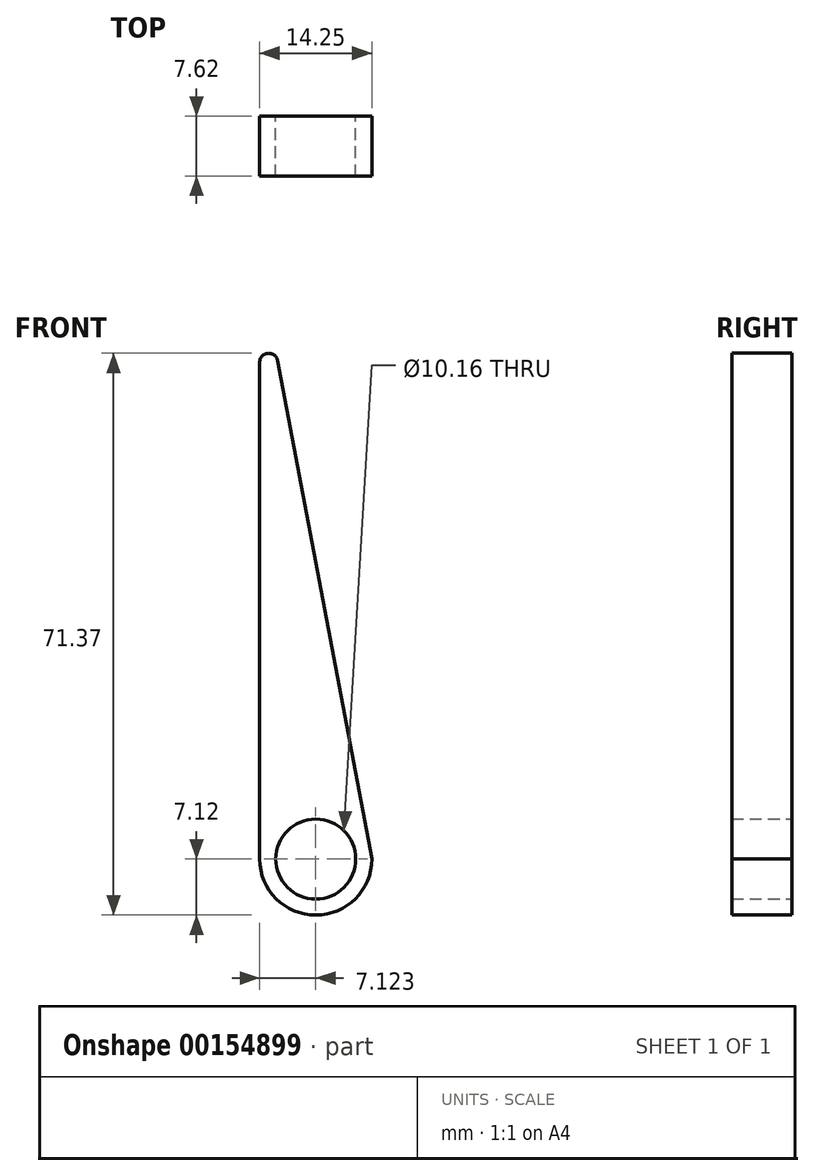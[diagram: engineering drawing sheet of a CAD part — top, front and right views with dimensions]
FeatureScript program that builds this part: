
annotation { "Feature Type Name" : "Feature", "Feature Type Description" : "" }
export const myFeature = defineFeature(function(context is Context, id is Id, definition is map)
    precondition{}
    {
        {
            var Q0;
            Q0=qCreatedBy(makeId("Front.planeOp"),FACE);
            var sketch = newSketch(context, id + "F0", { "sketchPlane" : qUnion([Q0])});
            skLineSegment(sketch, "E0", {"start": v(0, 0) * mm, "end": v(0, 75.39) * mm});
            skArc(sketch, "E1", {"start": v(0, 0) * mm, "mid": v(7.12, -7.12) * mm, "end": v(14.25, 0) * mm});
            skCircle(sketch, "E2", {"center": v(7.12, 0) * mm, "radius": 5.08 * mm});
            skLineSegment(sketch, "E3", {"start": v(14.25, 0) * mm, "end": v(0, 75.39) * mm});
            skSolve(sketch);
        }
        {
            var Q0;
            Q0=makeQuery(id+"F0.imprint","IMPRINT",FACE,{"disambiguationData":[TD([[makeQuery(id+"F0.imprint","IMPRINT",EDGE,{"derivedFrom":sQuery(id+"F0.wireOp",EDGE,"E0")}),-1.0]])]});
            extrude(context, id + "F1", {"entities" : qUnion([Q0]), "depth" : 7.62 * mm});
        }
        {
            var Q0;
            Q0=makeQuery(id+"F1.opExtrude","SWEPT_EDGE",EDGE,{"disambiguationData":[OSD([sQuery(id+"F0.wireOp",EDGE,"E0"),sQuery(id+"F0.wireOp",EDGE,"E3")])]});
            fillet(context, id + "F2", {"entities" : qUnion([Q0]), "radius" : 1.15 * mm, "tangentPropagation" : true, "allowEdgeOverflow" : false});
        }
    });
